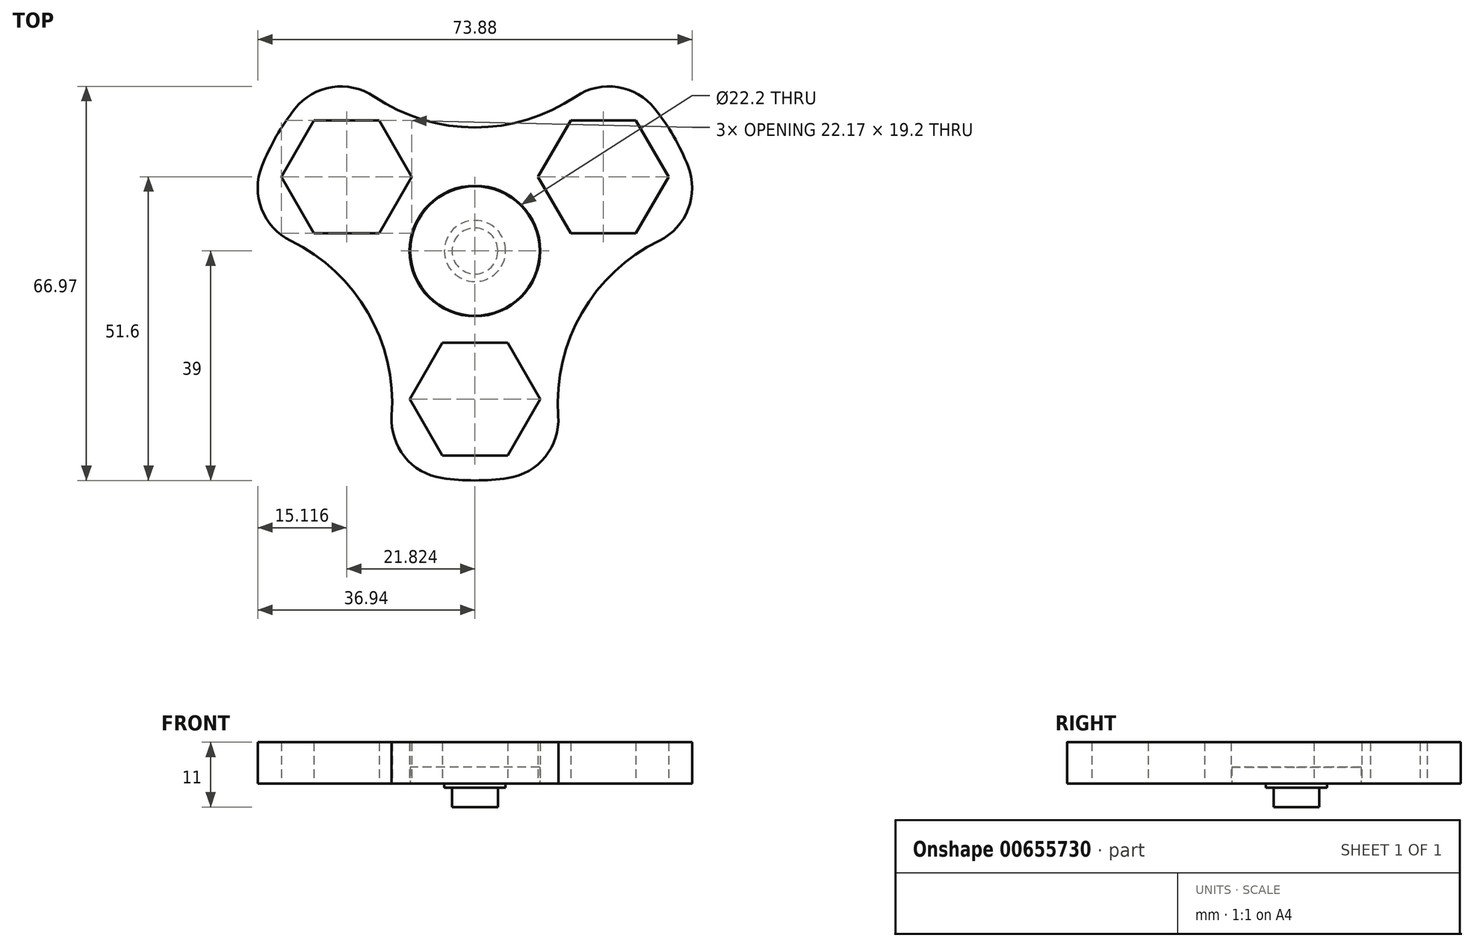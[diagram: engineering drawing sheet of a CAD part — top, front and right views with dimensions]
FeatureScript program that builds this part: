
annotation { "Feature Type Name" : "Feature", "Feature Type Description" : "" }
export const myFeature = defineFeature(function(context is Context, id is Id, definition is map)
    precondition{}
    {
        {
            var Q0;
            Q0=qCreatedBy(makeId("Top.planeOp"),FACE);
            var sketch = newSketch(context, id + "F0", { "sketchPlane" : qUnion([Q0])});
            skArc(sketch, "E0", {"start": v(38.77, 4.25) * mm, "mid": v(33.77, 19.5) * mm, "end": v(23.06, 31.45) * mm});
            skCircle(sketch, "E1", {"center": v(0, 0) * mm, "radius": 11.1 * mm});
            skLineSegment(sketch, "E2", {"start": v(0, 0) * mm, "end": v(0, -25.2) * mm, "construction": true});
            skCircle(sketch, "E3.cCircle", {"center": v(0, -25.2) * mm, "radius": 9.6 * mm, "construction": true});
            skLineSegment(sketch, "E3.0", {"start": v(5.54, -15.6) * mm, "end": v(11.09, -25.2) * mm});
            skLineSegment(sketch, "E3.1", {"start": v(11.09, -25.2) * mm, "end": v(5.54, -34.8) * mm});
            skLineSegment(sketch, "E3.2", {"start": v(5.54, -34.8) * mm, "end": v(-5.54, -34.8) * mm});
            skLineSegment(sketch, "E3.3", {"start": v(-5.54, -34.8) * mm, "end": v(-11.09, -25.2) * mm});
            skLineSegment(sketch, "E3.4", {"start": v(-11.09, -25.2) * mm, "end": v(-5.54, -15.6) * mm});
            skLineSegment(sketch, "E3.5", {"start": v(-5.54, -15.6) * mm, "end": v(5.54, -15.6) * mm});
            skPoint(sketch, "E3.0.midPoint", {"position": v(8.31, -20.4) * mm});
            skLineSegment(sketch, "E4", {"start": v(0, 0) * mm, "end": v(30, 0) * mm, "construction": true});
            skLineSegment(sketch, "E5", {"start": v(0, 0) * mm, "end": v(-15.7, -35.7) * mm, "construction": true});
            skLineSegment(sketch, "E6", {"start": v(0, 0) * mm, "end": v(15.7, -35.7) * mm, "construction": true});
            skLineSegment(sketch, "E7.1.0", {"start": v(-32.9, 12.6) * mm, "end": v(-27.37, 22.2) * mm});
            skLineSegment(sketch, "E7.1.1", {"start": v(-27.37, 3) * mm, "end": v(-32.9, 12.6) * mm});
            skLineSegment(sketch, "E7.1.2", {"start": v(-16.28, 3) * mm, "end": v(-27.37, 3) * mm});
            skLineSegment(sketch, "E7.1.3", {"start": v(-10.74, 12.6) * mm, "end": v(-16.28, 3) * mm});
            skLineSegment(sketch, "E7.1.4", {"start": v(-16.28, 22.2) * mm, "end": v(-10.74, 12.6) * mm});
            skLineSegment(sketch, "E7.1.5", {"start": v(-27.37, 22.2) * mm, "end": v(-16.28, 22.2) * mm});
            skLineSegment(sketch, "E7.1.6", {"start": v(0, 0) * mm, "end": v(-23.06, 31.45) * mm, "construction": true});
            skLineSegment(sketch, "E7.1.7", {"start": v(0, 0) * mm, "end": v(-38.77, 4.25) * mm, "construction": true});
            skLineSegment(sketch, "E7.2.0", {"start": v(27.37, 22.2) * mm, "end": v(32.9, 12.6) * mm});
            skLineSegment(sketch, "E7.2.1", {"start": v(16.28, 22.2) * mm, "end": v(27.37, 22.2) * mm});
            skLineSegment(sketch, "E7.2.2", {"start": v(10.74, 12.6) * mm, "end": v(16.28, 22.2) * mm});
            skLineSegment(sketch, "E7.2.3", {"start": v(16.28, 3) * mm, "end": v(10.74, 12.6) * mm});
            skLineSegment(sketch, "E7.2.4", {"start": v(27.37, 3) * mm, "end": v(16.28, 3) * mm});
            skLineSegment(sketch, "E7.2.5", {"start": v(32.9, 12.6) * mm, "end": v(27.37, 3) * mm});
            skLineSegment(sketch, "E7.2.6", {"start": v(0, 0) * mm, "end": v(38.77, 4.25) * mm, "construction": true});
            skLineSegment(sketch, "E7.2.7", {"start": v(0, 0) * mm, "end": v(23.06, 31.45) * mm, "construction": true});
            skLineSegment(sketch, "E7.anchor1", {"start": v(0, 0) * mm, "end": v(-5.54, -34.8) * mm, "construction": true});
            skLineSegment(sketch, "E7.anchor2", {"start": v(0, 0) * mm, "end": v(32.9, 12.6) * mm, "construction": true});
            skLineSegment(sketch, "E8", {"start": v(15.7, -35.7) * mm, "end": v(38.77, 4.25) * mm, "construction": true});
            skLineSegment(sketch, "E9", {"start": v(27.24, -15.72) * mm, "end": v(0, 0) * mm, "construction": true});
            skPoint(sketch, "E10", {"position": v(18.19, -10.5) * mm});
            skArc(sketch, "E11", {"start": v(38.77, 4.25) * mm, "mid": v(18.19, -10.5) * mm, "end": v(15.7, -35.7) * mm});
            skArc(sketch, "E12.1.0", {"start": v(-15.7, -35.7) * mm, "mid": v(-18.19, -10.5) * mm, "end": v(-38.77, 4.25) * mm});
            skArc(sketch, "E12.2.0", {"start": v(-23.06, 31.45) * mm, "mid": v(0, 21) * mm, "end": v(23.06, 31.45) * mm});
            skArc(sketch, "E13.trimOffspring", {"start": v(-23.06, 31.45) * mm, "mid": v(-33.77, 19.5) * mm, "end": v(-38.77, 4.25) * mm});
            skArc(sketch, "E14.trimOffspring", {"start": v(-15.7, -35.7) * mm, "mid": v(0, -39) * mm, "end": v(15.7, -35.7) * mm});
            skSolve(sketch);
        }
        {
            var Q0;
            Q0=makeQuery(id+"F0.imprint","IMPRINT",FACE,{"disambiguationData":[TD([[makeQuery(id+"F0.imprint","IMPRINT",EDGE,{"derivedFrom":sQuery(id+"F0.wireOp",EDGE,"E0")}),1.0]])]});
            extrude(context, id + "F1", {"entities" : qUnion([Q0]), "depth" : 7 * mm, "offsetDistance" : 25 * mm});
        }
        {
            var Q0;
            Q0=makeQuery(id+"F1.opExtrude","SWEPT_EDGE",EDGE,{"disambiguationData":[OSD([sQuery(id+"F0.wireOp",EDGE,"E12.1.0"),sQuery(id+"F0.wireOp",EDGE,"E13.trimOffspring")])]});
            var Q1;
            Q1=makeQuery(id+"F1.opExtrude","SWEPT_EDGE",EDGE,{"disambiguationData":[OSD([sQuery(id+"F0.wireOp",EDGE,"E12.2.0"),sQuery(id+"F0.wireOp",EDGE,"E13.trimOffspring")])]});
            var Q2;
            Q2=makeQuery(id+"F1.opExtrude","SWEPT_EDGE",EDGE,{"disambiguationData":[OSD([sQuery(id+"F0.wireOp",EDGE,"E0"),sQuery(id+"F0.wireOp",EDGE,"E12.2.0")])]});
            var Q3;
            Q3=makeQuery(id+"F1.opExtrude","SWEPT_EDGE",EDGE,{"disambiguationData":[OSD([sQuery(id+"F0.wireOp",EDGE,"E0"),sQuery(id+"F0.wireOp",EDGE,"E11")])]});
            var Q4;
            Q4=makeQuery(id+"F1.opExtrude","SWEPT_EDGE",EDGE,{"disambiguationData":[OSD([sQuery(id+"F0.wireOp",EDGE,"E11"),sQuery(id+"F0.wireOp",EDGE,"E14.trimOffspring")])]});
            var Q5;
            Q5=makeQuery(id+"F1.opExtrude","SWEPT_EDGE",EDGE,{"disambiguationData":[OSD([sQuery(id+"F0.wireOp",EDGE,"E12.1.0"),sQuery(id+"F0.wireOp",EDGE,"E14.trimOffspring")])]});
            fillet(context, id + "F2", {"entities" : qUnion([Q0, Q1, Q2, Q3, Q4, Q5]), "radius" : 10 * mm, "tangentPropagation" : true, "allowEdgeOverflow" : false});
        }
        {
            var Q0;
            Q0=qCreatedBy(makeId("Top.planeOp"),FACE);
            var sketch = newSketch(context, id + "F3", { "sketchPlane" : qUnion([Q0])});
            skCircle(sketch, "E15", {"center": v(0, 0) * mm, "radius": 3.9 * mm});
            skCircle(sketch, "E16", {"center": v(0, 0) * mm, "radius": 11 * mm});
            skSolve(sketch);
        }
        {
            var Q0;
            Q0=makeQuery(id+"F3.imprint","IMPRINT",FACE,{"disambiguationData":[TD([[makeQuery(id+"F3.imprint","IMPRINT",EDGE,{"derivedFrom":sQuery(id+"F3.wireOp",EDGE,"E15")}),1.0]])]});
            var Q1;
            Q1=makeQuery(id+"F3.imprint","IMPRINT",FACE,{"disambiguationData":[TD([[makeQuery(id+"F3.imprint","IMPRINT",EDGE,{"derivedFrom":sQuery(id+"F3.wireOp",EDGE,"E15")}),-1.0]])]});
            extrude(context, id + "F4", {"entities" : qUnion([Q0, Q1]), "depth" : 2.8 * mm, "offsetDistance" : 25 * mm});
        }
        {
            var Q0;
            Q0=makeQuery(id+"F3.imprint","IMPRINT",FACE,{"disambiguationData":[TD([[makeQuery(id+"F3.imprint","IMPRINT",EDGE,{"derivedFrom":sQuery(id+"F3.wireOp",EDGE,"E15")}),1.0]])]});
            extrude(context, id + "F5", {"entities" : qUnion([Q0]), "operationType" : NewBodyOperationType.ADD, "oppositeDirection" : true, "depth" : 4 * mm, "offsetDistance" : 25 * mm});
        }
        {
            var Q0;
            Q0=makeQuery(id+"F3.imprint","IMPRINT",FACE,{"disambiguationData":[TD([[makeQuery(id+"F3.imprint","IMPRINT",EDGE,{"derivedFrom":sQuery(id+"F3.wireOp",EDGE,"E15")}),-1.0]])]});
            var sketch = newSketch(context, id + "F6", { "sketchPlane" : qUnion([Q0])});
            skCircle(sketch, "E17", {"center": v(0, 0) * mm, "radius": 5.2 * mm});
            skSolve(sketch);
        }
        {
            var Q0;
            Q0=makeQuery(id+"F6.imprint","IMPRINT",FACE,{"disambiguationData":[TD([[makeQuery(id+"F6.imprint","IMPRINT",EDGE,{"derivedFrom":sQuery(id+"F6.wireOp",EDGE,"E17")}),1.0]])]});
            extrude(context, id + "F7", {"entities" : qUnion([Q0]), "operationType" : NewBodyOperationType.ADD, "oppositeDirection" : true, "depth" : 0.75 * mm, "offsetDistance" : 25 * mm});
        }
    });
